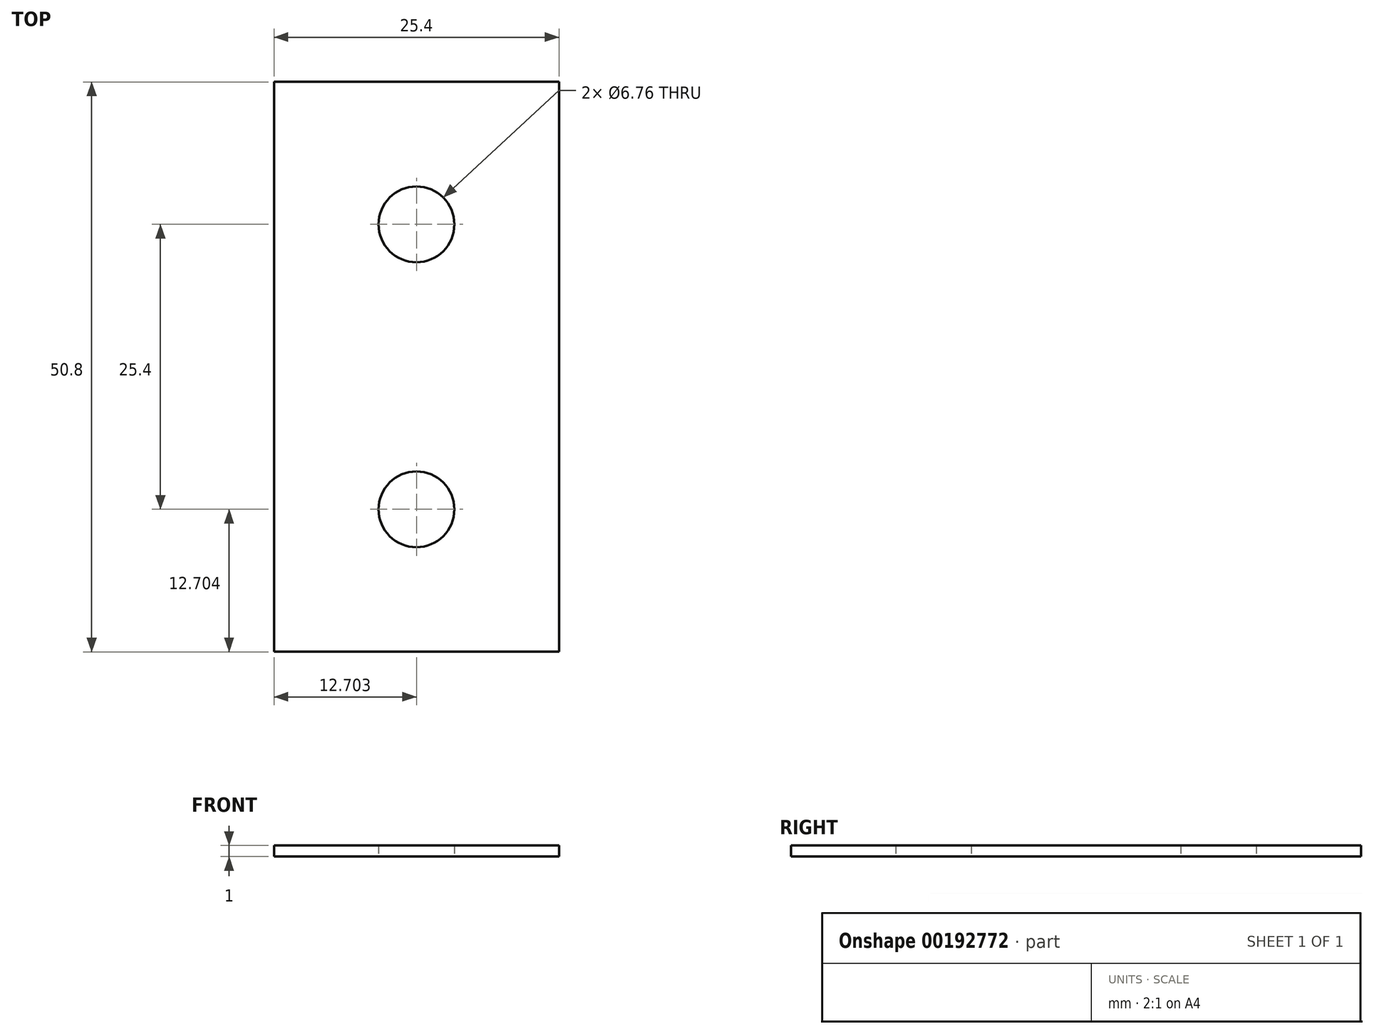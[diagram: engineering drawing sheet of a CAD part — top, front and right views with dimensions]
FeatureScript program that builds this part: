
annotation { "Feature Type Name" : "Feature", "Feature Type Description" : "" }
export const myFeature = defineFeature(function(context is Context, id is Id, definition is map)
    precondition{}
    {
        {
            var Q0;
            Q0=qCreatedBy(makeId("Top.planeOp"),FACE);
            var sketch = newSketch(context, id + "F0", { "sketchPlane" : qUnion([Q0])});
            skLineSegment(sketch, "E0.bottom", {"start": v(-49.97, 36.53) * mm, "end": v(-24.57, 36.53) * mm});
            skLineSegment(sketch, "E0.top", {"start": v(-49.97, -14.27) * mm, "end": v(-24.57, -14.27) * mm});
            skLineSegment(sketch, "E0.left", {"start": v(-49.97, 36.53) * mm, "end": v(-49.97, -14.27) * mm});
            skLineSegment(sketch, "E0.right", {"start": v(-24.57, 36.53) * mm, "end": v(-24.57, -14.27) * mm});
            skCircle(sketch, "E1", {"center": v(-37.27, 23.83) * mm, "radius": 3.38 * mm});
            skCircle(sketch, "E2", {"center": v(-37.27, -1.57) * mm, "radius": 3.38 * mm});
            skSolve(sketch);
        }
        {
            var Q0;
            Q0=makeQuery(id+"F0.imprint","IMPRINT",FACE,{"disambiguationData":[TD([[makeQuery(id+"F0.imprint","IMPRINT",EDGE,{"derivedFrom":sQuery(id+"F0.wireOp",EDGE,"E0.bottom")}),-1.0]])]});
            extrude(context, id + "F1", {"entities" : qUnion([Q0]), "depth" : 1 * mm});
        }
    });
